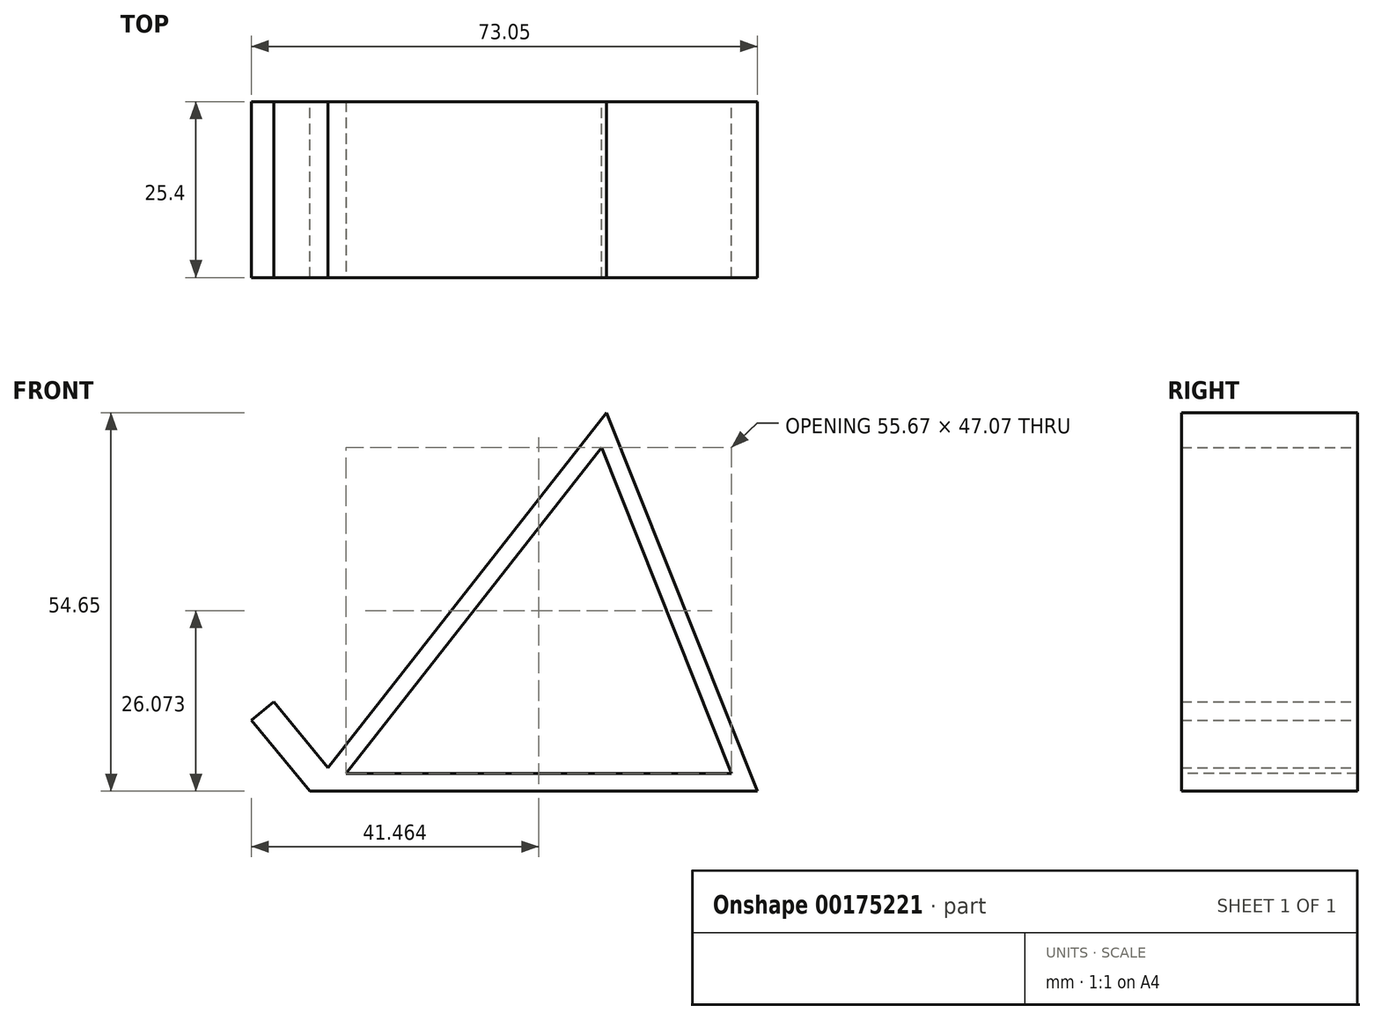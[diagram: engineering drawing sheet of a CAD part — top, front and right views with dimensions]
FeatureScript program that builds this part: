
annotation { "Feature Type Name" : "Feature", "Feature Type Description" : "" }
export const myFeature = defineFeature(function(context is Context, id is Id, definition is map)
    precondition{}
    {
        {
            var Q0;
            Q0=qCreatedBy(makeId("Front.planeOp"),FACE);
            var sketch = newSketch(context, id + "F0", { "sketchPlane" : qUnion([Q0])});
            skLineSegment(sketch, "E0", {"start": v(0, 37.18) * mm, "end": v(-42.83, -17.47) * mm});
            skLineSegment(sketch, "E1", {"start": v(-42.83, -17.47) * mm, "end": v(-51.24, -7.23) * mm});
            skLineSegment(sketch, "E2", {"start": v(-51.24, -7.23) * mm, "end": v(-47.98, -4.55) * mm});
            skLineSegment(sketch, "E3", {"start": v(-47.98, -4.55) * mm, "end": v(-40.17, -14.08) * mm});
            skLineSegment(sketch, "E4", {"start": v(0, 37.18) * mm, "end": v(21.8, -17.47) * mm});
            skLineSegment(sketch, "E5", {"start": v(21.8, -17.47) * mm, "end": v(-42.83, -17.47) * mm});
            skSolve(sketch);
        }
        {
            var Q0;
            {var subQ0=sQuery(id+"F0.wireOp",EDGE,"E4");Q0=makeQuery(id+"F0.imprint","IMPRINT",FACE,{"disambiguationData":[TD([[makeQuery(id+"F0.imprint","IMPRINT",EDGE,{"derivedFrom":subQ0}),-1.0]])]});}
            var Q1;
            {var subQ0=sQuery(id+"F0.wireOp",EDGE,"E1");Q1=makeQuery(id+"F0.imprint","IMPRINT",FACE,{"disambiguationData":[TD([[makeQuery(id+"F0.imprint","IMPRINT",EDGE,{"derivedFrom":subQ0}),-1.0]])]});}
            extrude(context, id + "F1", {"entities" : qUnion([Q0, Q1]), "depth" : 25.4 * mm});
        }
        {
            var Q0;
            Q0=makeQuery(id+"F1.opExtrude","CAP_FACE",FACE,{"disambiguationData":[OSD([sQuery(id+"F0.wireOp",EDGE,"E0"),sQuery(id+"F0.wireOp",EDGE,"E1"),sQuery(id+"F0.wireOp",EDGE,"E2"),sQuery(id+"F0.wireOp",EDGE,"E3"),sQuery(id+"F0.wireOp",EDGE,"E4"),sQuery(id+"F0.wireOp",EDGE,"E5")])],"isStart":false});
            var Q1;
            Q1=makeQuery(id+"F1.opExtrude","CAP_FACE",FACE,{"disambiguationData":[OSD([sQuery(id+"F0.wireOp",EDGE,"E0"),sQuery(id+"F0.wireOp",EDGE,"E1"),sQuery(id+"F0.wireOp",EDGE,"E2"),sQuery(id+"F0.wireOp",EDGE,"E3"),sQuery(id+"F0.wireOp",EDGE,"E4"),sQuery(id+"F0.wireOp",EDGE,"E5")])],"isStart":true});
            shell(context, id + "F2", {"entities" : qUnion([Q0, Q1]), "thickness" : 2.54 * mm});
        }
    });
